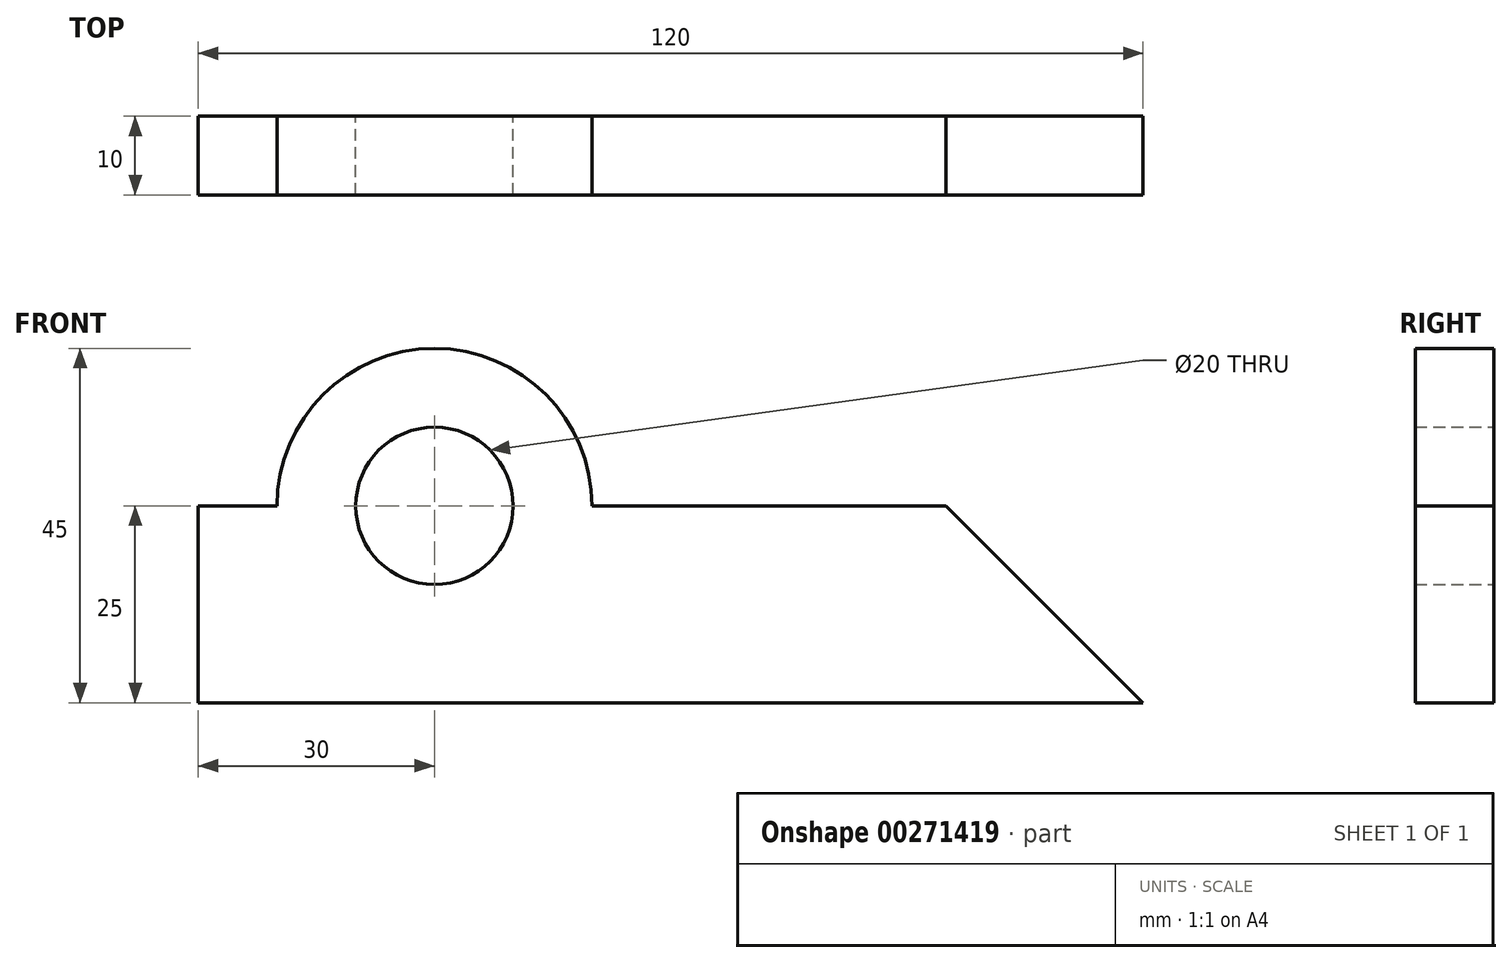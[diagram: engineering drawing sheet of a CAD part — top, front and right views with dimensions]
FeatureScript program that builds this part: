
annotation { "Feature Type Name" : "Feature", "Feature Type Description" : "" }
export const myFeature = defineFeature(function(context is Context, id is Id, definition is map)
    precondition{}
    {
        {
            var Q0;
            Q0=qCreatedBy(makeId("Front.planeOp"),FACE);
            var sketch = newSketch(context, id + "F0", { "sketchPlane" : qUnion([Q0])});
            skLineSegment(sketch, "E0", {"start": v(0, 0) * mm, "end": v(0, 25) * mm});
            skLineSegment(sketch, "E1", {"start": v(0, 0) * mm, "end": v(120, 0) * mm});
            skLineSegment(sketch, "E2", {"start": v(95, 25) * mm, "end": v(120, 0) * mm});
            skLineSegment(sketch, "E3", {"start": v(0, 25) * mm, "end": v(10, 25) * mm});
            skLineSegment(sketch, "E4", {"start": v(95, 25) * mm, "end": v(50, 25) * mm});
            skArc(sketch, "E5", {"start": v(50, 25) * mm, "mid": v(30, 45) * mm, "end": v(10, 25) * mm});
            skCircle(sketch, "E6", {"center": v(30, 25) * mm, "radius": 10 * mm});
            skSolve(sketch);
        }
        {
            var Q0;
            Q0=makeQuery(id+"F0.imprint","IMPRINT",FACE,{"disambiguationData":[TD([[makeQuery(id+"F0.imprint","IMPRINT",EDGE,{"derivedFrom":sQuery(id+"F0.wireOp",EDGE,"E0")}),-1.0]])]});
            extrude(context, id + "F1", {"entities" : qUnion([Q0]), "depth" : 10 * mm});
        }
    });
